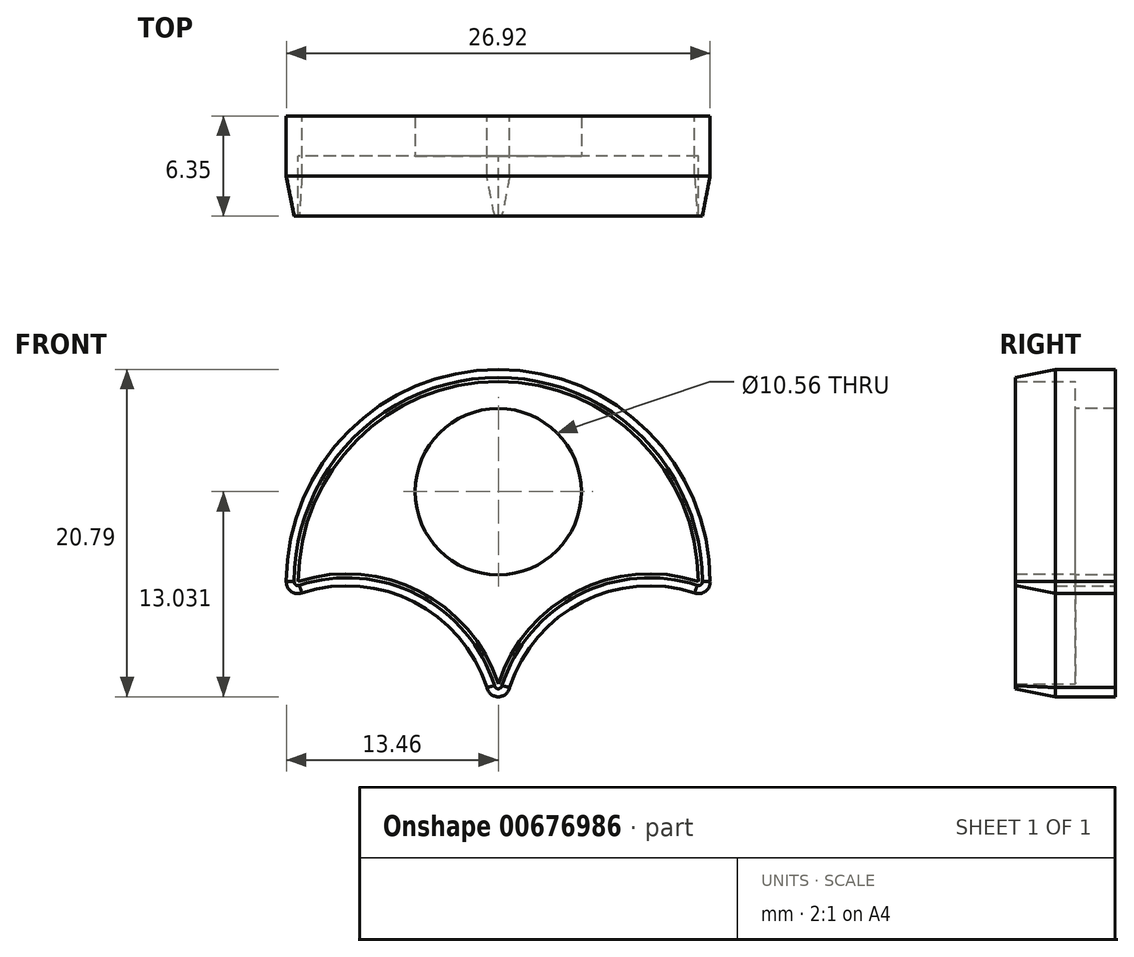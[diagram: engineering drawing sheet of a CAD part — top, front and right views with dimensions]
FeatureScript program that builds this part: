
annotation { "Feature Type Name" : "Feature", "Feature Type Description" : "" }
export const myFeature = defineFeature(function(context is Context, id is Id, definition is map)
    precondition{}
    {
        {
            var Q0;
            Q0=qCreatedBy(makeId("Front.planeOp"),FACE);
            var sketch = newSketch(context, id + "F0", { "sketchPlane" : qUnion([Q0])});
            skArc(sketch, "E0", {"start": v(12.7, 0) * mm, "mid": v(0, 12.7) * mm, "end": v(-12.7, 0) * mm});
            skArc(sketch, "E1", {"start": v(0, -6.5) * mm, "mid": v(-5, -0.62) * mm, "end": v(-12.7, 0) * mm});
            skArc(sketch, "E2.MirrorCS", {"start": v(0, -6.5) * mm, "mid": v(5, -0.62) * mm, "end": v(12.7, 0) * mm});
            skPoint(sketch, "E3.orphan", {"position": v(0, -12.7) * mm});
            skArc(sketch, "E4.0", {"start": v(13.46, 0) * mm, "mid": v(0, 13.46) * mm, "end": v(-13.46, 0) * mm});
            skArc(sketch, "E5.0", {"start": v(-0.73, -6.74) * mm, "mid": v(-5.35, -1.3) * mm, "end": v(-12.47, -0.73) * mm});
            skArc(sketch, "E6.0", {"start": v(0.73, -6.74) * mm, "mid": v(5.35, -1.3) * mm, "end": v(12.47, -0.73) * mm});
            skArc(sketch, "E7", {"start": v(-0.73, -6.74) * mm, "mid": v(0, -7.33) * mm, "end": v(0.73, -6.74) * mm});
            skArc(sketch, "E8", {"start": v(-13.46, 0) * mm, "mid": v(-13.16, -0.63) * mm, "end": v(-12.47, -0.73) * mm});
            skArc(sketch, "E9", {"start": v(12.47, -0.73) * mm, "mid": v(13.16, -0.63) * mm, "end": v(13.46, 0) * mm});
            skSolve(sketch);
        }
        {
            var Q0;
            Q0 = qSketchRegion(id + "F0", true);
            extrude(context, id + "F1", {"entities" : qUnion([Q0]), "depth" : 6.35 * mm, "offsetDistance" : 25.4 * mm});
        }
        {
            var Q0;
            Q0=qCreatedBy(makeId("Front.planeOp"),FACE);
            var sketch = newSketch(context, id + "F2", { "sketchPlane" : qUnion([Q0])});
            skArc(sketch, "E10.0", {"start": v(12.7, 0) * mm, "mid": v(0, 12.7) * mm, "end": v(-12.7, 0) * mm});
            skArc(sketch, "E11.0", {"start": v(0, -6.5) * mm, "mid": v(-5, -0.62) * mm, "end": v(-12.7, 0) * mm});
            skArc(sketch, "E12.0", {"start": v(0, -6.5) * mm, "mid": v(5, -0.62) * mm, "end": v(12.7, 0) * mm});
            skSolve(sketch);
        }
        {
            var Q0;
            Q0=makeQuery(id+"F2.imprint","IMPRINT",FACE,{"disambiguationData":[TD([[makeQuery(id+"F2.imprint","IMPRINT",EDGE,{"derivedFrom":sQuery(id+"F2.wireOp",EDGE,"E10.0")}),1.0]])]});
            extrude(context, id + "F3", {"entities" : qUnion([Q0]), "operationType" : NewBodyOperationType.ADD, "depth" : 2.54 * mm, "offsetDistance" : 25.4 * mm});
        }
        {
            var Q0;
            Q0=makeQuery(id+"F3.opExtrude","CAP_FACE",FACE,{"disambiguationData":[OSD([sQuery(id+"F2.wireOp",EDGE,"E10.0"),sQuery(id+"F2.wireOp",EDGE,"E11.0"),sQuery(id+"F2.wireOp",EDGE,"E12.0")])],"isStart":false});
            var sketch = newSketch(context, id + "F4", { "sketchPlane" : qUnion([Q0])});
            skCircle(sketch, "E13", {"center": v(0, 5.7) * mm, "radius": 5.28 * mm});
            skSolve(sketch);
        }
        {
            var Q0;
            Q0 = qSketchRegion(id + "F4", true);
            extrude(context, id + "F5", {"entities" : qUnion([Q0]), "operationType" : NewBodyOperationType.REMOVE, "oppositeDirection" : true, "depth" : 25.4 * mm, "offsetDistance" : 25.4 * mm});
        }
        {
            var Q0;
            Q0=makeQuery(id+"F1.opExtrude","CAP_EDGE",EDGE,{"disambiguationData":[OSD([sQuery(id+"F0.wireOp",EDGE,"E4.0")])],"isStart":false});
            var Q1;
            Q1=makeQuery(id+"F1.opExtrude","CAP_EDGE",EDGE,{"disambiguationData":[OSD([sQuery(id+"F0.wireOp",EDGE,"E7")])],"isStart":false});
            var Q2;
            Q2=makeQuery(id+"F1.opExtrude","CAP_EDGE",EDGE,{"disambiguationData":[OSD([sQuery(id+"F0.wireOp",EDGE,"E6.0")])],"isStart":false});
            var Q3;
            Q3=makeQuery(id+"F1.opExtrude","CAP_EDGE",EDGE,{"disambiguationData":[OSD([sQuery(id+"F0.wireOp",EDGE,"E9")])],"isStart":false});
            var Q4;
            Q4=makeQuery(id+"F1.opExtrude","CAP_EDGE",EDGE,{"disambiguationData":[OSD([sQuery(id+"F0.wireOp",EDGE,"E8")])],"isStart":false});
            var Q5;
            Q5=makeQuery(id+"F1.opExtrude","CAP_EDGE",EDGE,{"disambiguationData":[OSD([sQuery(id+"F0.wireOp",EDGE,"E5.0")])],"isStart":false});
            chamfer(context, id + "F6", {"entities" : qUnion([Q0, Q1, Q2, Q3, Q4, Q5]), "chamferType" : ChamferType.TWO_OFFSETS, "width1" : 0.5 * mm, "oppositeDirection" : false, "width2" : 2.54 * mm, "tangentPropagation" : true});
        }
    });
